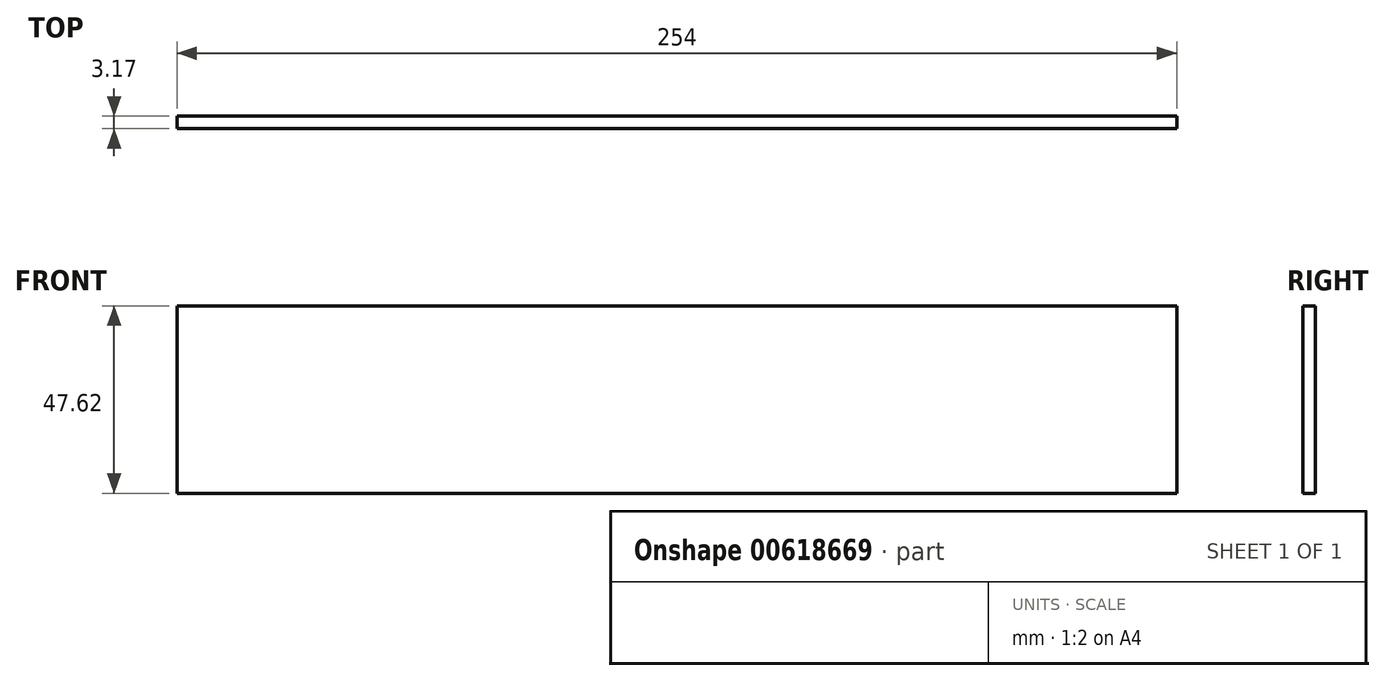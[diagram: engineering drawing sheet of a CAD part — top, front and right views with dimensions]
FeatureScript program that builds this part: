
annotation { "Feature Type Name" : "Feature", "Feature Type Description" : "" }
export const myFeature = defineFeature(function(context is Context, id is Id, definition is map)
    precondition{}
    {
        {
            var Q0;
            Q0=qCreatedBy(makeId("Front.planeOp"),FACE);
            var sketch = newSketch(context, id + "F0", { "sketchPlane" : qUnion([Q0])});
            skLineSegment(sketch, "E0.bottom", {"start": v(0, 0) * mm, "end": v(254, 0) * mm});
            skLineSegment(sketch, "E0.top", {"start": v(0, 47.63) * mm, "end": v(254, 47.63) * mm});
            skLineSegment(sketch, "E0.left", {"start": v(0, 0) * mm, "end": v(0, 47.63) * mm});
            skLineSegment(sketch, "E0.right", {"start": v(254, 0) * mm, "end": v(254, 47.63) * mm});
            skSolve(sketch);
        }
        {
            var Q0;
            Q0=makeQuery(id+"F0.imprint","IMPRINT",FACE,{"disambiguationData":[TD([[makeQuery(id+"F0.imprint","IMPRINT",EDGE,{"derivedFrom":sQuery(id+"F0.wireOp",EDGE,"E0.bottom")}),1.0]])]});
            extrude(context, id + "F1", {"entities" : qUnion([Q0]), "depth" : 3.17 * mm, "offsetDistance" : 25.4 * mm});
        }
    });
